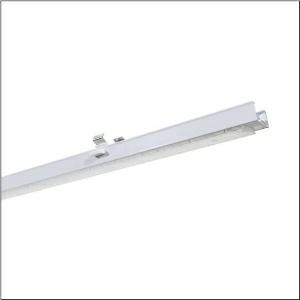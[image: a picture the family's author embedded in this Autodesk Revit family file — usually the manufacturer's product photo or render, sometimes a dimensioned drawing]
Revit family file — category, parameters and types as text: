
# Revit family: sanierungs-leuchteneinsatz_31_gen_2_51re11db4cb_15df
name_source: partatom
category: Lighting Fixtures
units: mm (PartAtom-declared; Revit-internal decimal feet)

## family parameters
Cut with Voids When Loaded = No
Host = Face
Light Source = No
Part Type = Normal
Room Calculation Point = No
Round Connector Dimension = Use Diameter
Shared = No

## types (1)
- Sanierungs-Leuchteneinsatz 31 Gen.2 (1 x LED, 11500 lm, 66 W, 4000K)
    Apparent Load = 66 VA
    CIE Flux Codes = 83 93 98 100 100
    Color Rendering = 80
    Color Temperature = 4000K
    Default Elevation = 1800 mm
    Description = Refurbishment luminaire insert Gen.2, luminaire insert, of extruded aluminium section, coated, traffic white (RAL 9016), length: 1.472mm, width: 91mm, height: 53mm, LED rated luminous flux: 11.500lm, light colour: 840, control gear: DALI 2, with system connector: socket, mains connection: 220..240V, AC, 50/60Hz, primary light control with lens, of plastic, primary optical cover: cover, of PMMA, light emission: direct distribution, protection rating (complete): IP20, insulation class (complete): insulation class I (protective earthing), certification: CE, UKCA, impact resistance: IK02, permissible ambient temperature for indoor applications: -20..+40°C, packaging unit: 1 piece
    Height = 58 mm
    Lamp = 1 x LED
    Lamp Light Flux = 11500 lm
    Lamp Power = 66 W
    Lamp count = 1
    Length = 1472 mm
    Luminous efficacy = 174 lm/W
    Manufacturer = Siteco
    ModVariant = No
    Model = 51RE11DB4CB
    Mounting Place = Ceiling
    Mounting Type = Pendant
    Number of Poles = 1
    OnlyDefault = Yes
    Power Factor = 1
    Product Name = Sanierungs-Leuchteneinsatz 31 Gen.2
    Product group = luminaire insert
    ProductGroupID = 902
    Protection Class = Protection class I
    Protection Degree = IP 20
    RLX_Detail_Level = 1
    RlxData = <blob elided: 19469 chars, md5=c36f2c12>
    Socket = socket
    Standby Power = 0 W
    System Light Flux = 11500 lm
    System Power = 66 W
    Type Comments = Product without accessories
    Type Image = l_1266702.jpg
    URL = http://relux.com
    VarID = ---
    Voltage = 0 V
    Weight = 0.00 kg
    Width = 65 mm

## geometry (parser evidence)
native form markers: Blend x4, Sweep x12
no freeform markers — native parametric forms only
